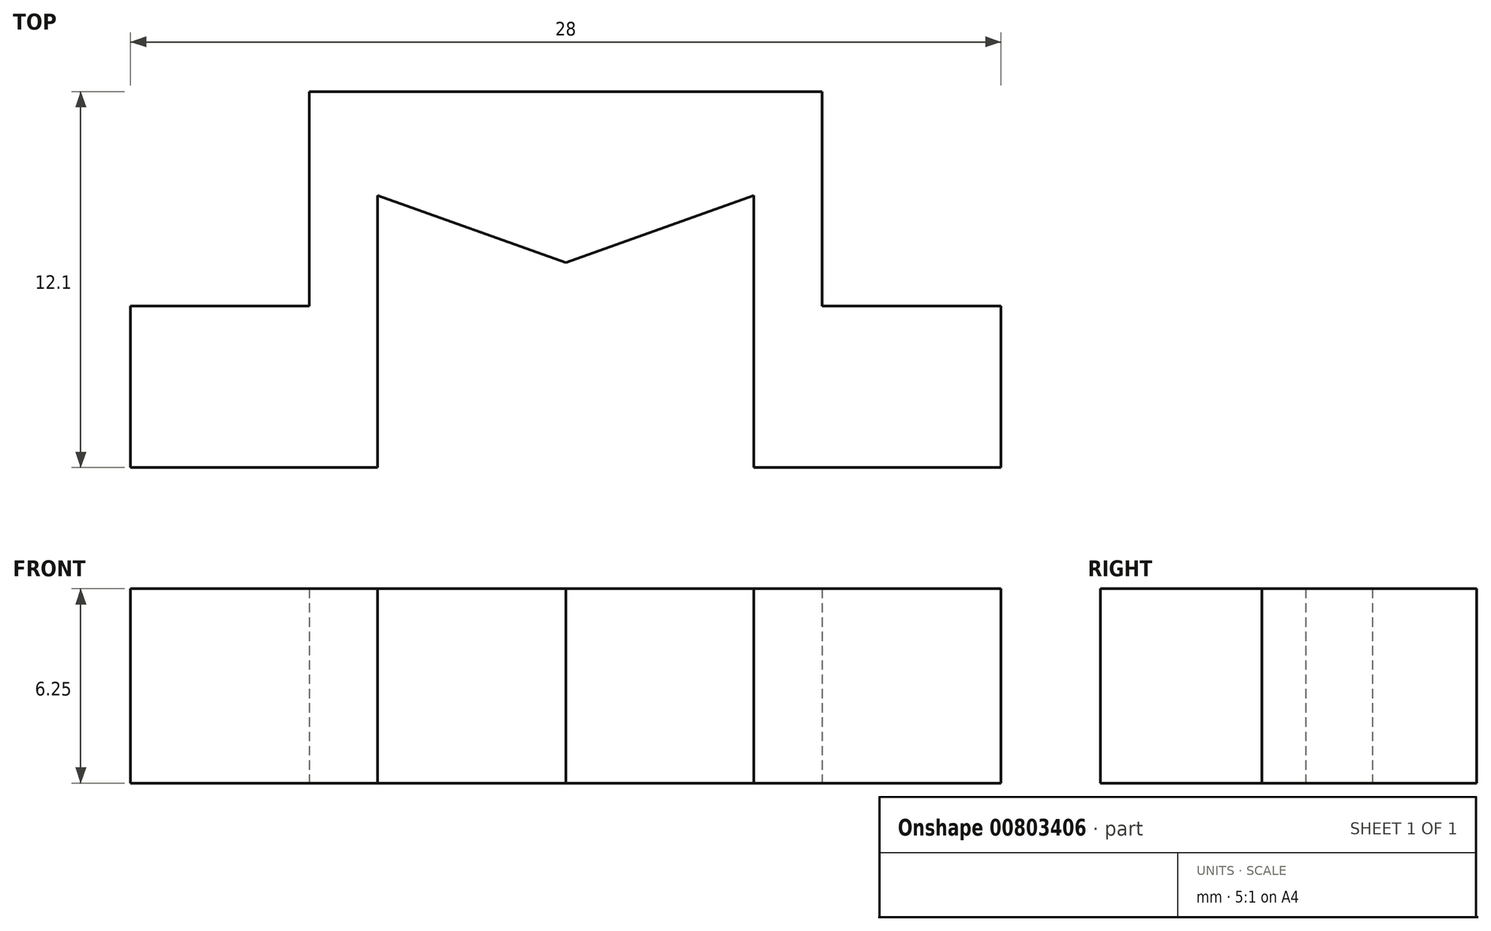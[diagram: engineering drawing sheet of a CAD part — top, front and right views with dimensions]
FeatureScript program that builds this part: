
annotation { "Feature Type Name" : "Feature", "Feature Type Description" : "" }
export const myFeature = defineFeature(function(context is Context, id is Id, definition is map)
    precondition{}
    {
        {
            var Q0;
            Q0=qCreatedBy(makeId("Top.planeOp"),FACE);
            var sketch = newSketch(context, id + "F0", { "sketchPlane" : qUnion([Q0])});
            skLineSegment(sketch, "E0", {"start": v(0, 12.1) * mm, "end": v(8.25, 12.1) * mm});
            skLineSegment(sketch, "E1", {"start": v(8.25, 12.1) * mm, "end": v(8.25, 5.2) * mm});
            skLineSegment(sketch, "E2", {"start": v(8.25, 5.2) * mm, "end": v(14, 5.2) * mm});
            skLineSegment(sketch, "E3", {"start": v(14, 5.2) * mm, "end": v(14, 0) * mm});
            skLineSegment(sketch, "E4", {"start": v(14, 0) * mm, "end": v(6.05, 0) * mm});
            skLineSegment(sketch, "E5", {"start": v(6.05, 0) * mm, "end": v(6.05, 8.75) * mm});
            skLineSegment(sketch, "E6", {"start": v(6.05, 8.75) * mm, "end": v(0, 6.6) * mm});
            skLineSegment(sketch, "E7.MirrorCS", {"start": v(0, 12.1) * mm, "end": v(-8.25, 12.1) * mm});
            skLineSegment(sketch, "E8.MirrorCS", {"start": v(-8.25, 12.1) * mm, "end": v(-8.25, 5.2) * mm});
            skLineSegment(sketch, "E9.MirrorCS", {"start": v(-6.05, 8.75) * mm, "end": v(0, 6.6) * mm});
            skLineSegment(sketch, "E10.MirrorCS", {"start": v(-8.25, 5.2) * mm, "end": v(-14, 5.2) * mm});
            skLineSegment(sketch, "E11.MirrorCS", {"start": v(-14, 0) * mm, "end": v(-6.05, 0) * mm});
            skLineSegment(sketch, "E12.MirrorCS", {"start": v(-6.05, 0) * mm, "end": v(-6.05, 8.75) * mm});
            skLineSegment(sketch, "E13.MirrorCS", {"start": v(-14, 5.2) * mm, "end": v(-14, 0) * mm});
            skSolve(sketch);
        }
        {
            var Q0;
            Q0 = qSketchRegion(id + "F0", true);
            extrude(context, id + "F1", {"entities" : qUnion([Q0]), "depth" : 6.25 * mm, "offsetDistance" : 25 * mm});
        }
    });
